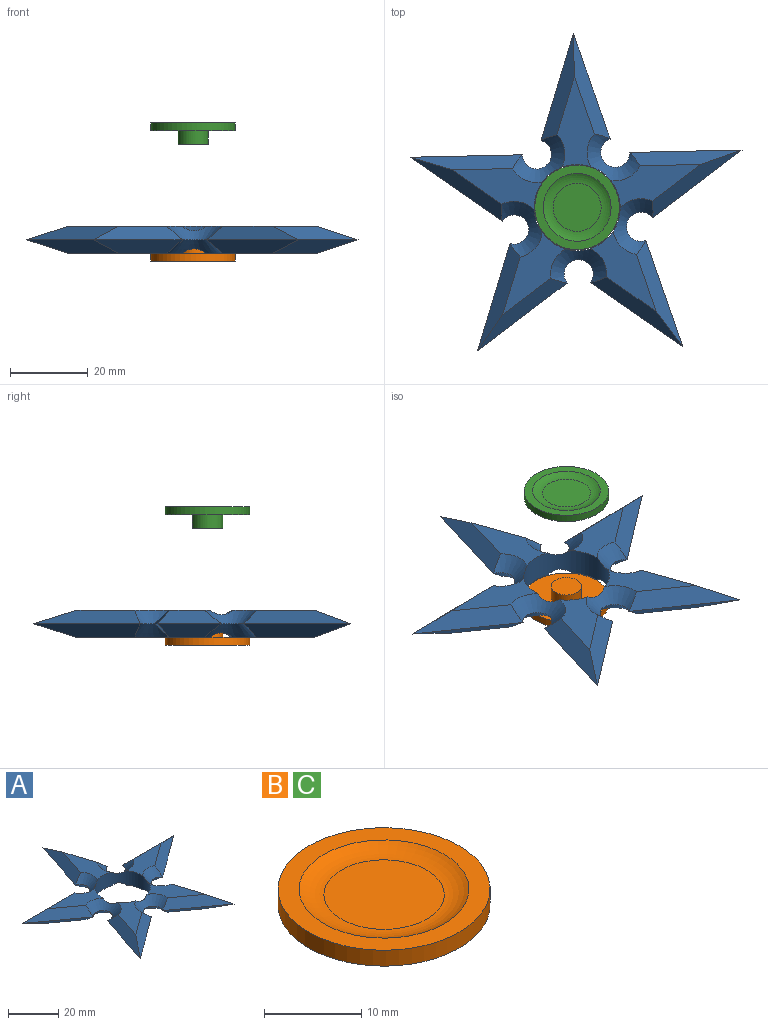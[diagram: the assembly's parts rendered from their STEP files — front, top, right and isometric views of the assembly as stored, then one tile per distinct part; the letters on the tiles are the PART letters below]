
ASSEMBLY  parts=3 mates=2
PART A: 41 faces, bbox 85.6x81.4x7 mm
  f0: plane 20.97x16.66mm, normal (0,0,-1), area 124.1mm2, adj f8,f27,f31,f35,f38
  f1: plane 23.23x10.72mm, normal (0,0,-1), area 124.1mm2, adj f8,f26,f30,f34,f38
  f2: plane 23.22x9.63mm, normal (0,0,-1), area 124.1mm2, adj f8,f14,f18,f22,f26
  f3: plane 23.23x10.72mm, normal (0,0,-1), area 124.1mm2, adj f8,f11,f12,f14,f15
  f4: plane 20.97x16.66mm, normal (0,0,1), area 124.1mm2, adj f8,f32,f36,f39,f40
  f5: plane 23.23x10.72mm, normal (0,0,1), area 124.1mm2, adj f8,f29,f33,f37,f40
  f6: plane 23.22x9.63mm, normal (0,0,1), area 124.1mm2, adj f8,f17,f21,f25,f29
  f7: plane 23.23x10.72mm, normal (0,0,1), area 124.1mm2, adj f8,f13,f16,f17,f20
  f8: cylinder r=11.1mm len=22.2mm, axis (0,0,-1), area 440mm2, adj f0,f1,f2,f3,f4,f5,f6,f7
  f9: plane 20.97x16.66mm, normal (0,0,1), area 124.1mm2, adj f8,f20,f24,f28,f32
  f10: plane 20.97x16.66mm, normal (0,0,-1), area 124.1mm2, adj f8,f15,f19,f23,f27
  f11: plane 28.94x3.5mm, normal (0,0.71,-0.71), area 109.6mm2, adj f3,f12,f13,f14
  f12: plane 23.42x17.01mm, normal (-0.42,-0.57,-0.71), area 109.6mm2, adj f3,f11,f15,f16
  f13: plane 28.94x3.5mm, normal (0,0.71,0.71), area 109.6mm2, adj f7,f11,f16,f17
  f14: cone r=7.25mm half-angle=45deg, axis (0,0,-1), area 95mm2, adj f2,f3,f8,f11,f17,f18
  f15: cone r=7.25mm half-angle=45deg, axis (0,0,-1), area 95mm2, adj f3,f8,f10,f12,f19,f20
  f16: plane 23.42x17.01mm, normal (-0.42,-0.57,0.71), area 109.6mm2, adj f7,f12,f13,f20
  f17: cone r=3.75mm half-angle=45deg, axis (0,0,1), area 95mm2, adj f6,f7,f8,f13,f14,f21
  f18: plane 27.53x8.94mm, normal (-0.67,0.22,-0.71), area 109.6mm2, adj f2,f14,f21,f22
  f19: plane 27.53x11.47mm, normal (-0.67,0.22,-0.71), area 109.6mm2, adj f10,f15,f23,f24
  f20: cone r=3.75mm half-angle=45deg, axis (0,0,1), area 95mm2, adj f7,f8,f9,f15,f16,f24
  f21: plane 27.53x8.94mm, normal (-0.67,0.22,0.71), area 109.6mm2, adj f6,f17,f18,f25
  f22: plane 27.53x8.94mm, normal (0.67,0.22,-0.71), area 109.6mm2, adj f2,f18,f25,f26
  f23: plane 23.42x18.32mm, normal (0.42,-0.57,-0.71), area 109.6mm2, adj f10,f19,f27,f28
  f24: plane 27.53x11.47mm, normal (-0.67,0.22,0.71), area 109.6mm2, adj f9,f19,f20,f28
  f25: plane 27.53x8.94mm, normal (0.67,0.22,0.71), area 109.6mm2, adj f6,f21,f22,f29
  f26: cone r=7.25mm half-angle=45deg, axis (0,0,-1), area 95mm2, adj f1,f2,f8,f22,f29,f30
  f27: cone r=7.25mm half-angle=45deg, axis (0,0,-1), area 95mm2, adj f0,f8,f10,f23,f31,f32
  f28: plane 23.42x18.32mm, normal (0.42,-0.57,0.71), area 109.6mm2, adj f9,f23,f24,f32
  f29: cone r=3.75mm half-angle=45deg, axis (0,0,1), area 95mm2, adj f5,f6,f8,f25,f26,f33
  f30: plane 28.94x3.5mm, normal (0,0.71,-0.71), area 109.6mm2, adj f1,f26,f33,f34
  f31: plane 23.42x18.32mm, normal (-0.42,-0.57,-0.71), area 109.6mm2, adj f0,f27,f35,f36
  f32: cone r=3.75mm half-angle=45deg, axis (0,0,1), area 95mm2, adj f4,f8,f9,f27,f28,f36
  f33: plane 28.94x3.5mm, normal (0,0.71,0.71), area 109.6mm2, adj f5,f29,f30,f37
  f34: plane 23.42x17.01mm, normal (0.42,-0.57,-0.71), area 109.6mm2, adj f1,f30,f37,f38
  f35: plane 27.53x11.47mm, normal (0.67,0.22,-0.71), area 109.6mm2, adj f0,f31,f38,f39
  f36: plane 23.42x18.32mm, normal (-0.42,-0.57,0.71), area 109.6mm2, adj f4,f31,f32,f39
  f37: plane 23.42x17.01mm, normal (0.42,-0.57,0.71), area 109.6mm2, adj f5,f33,f34,f40
  f38: cone r=7.25mm half-angle=45deg, axis (0,0,-1), area 95mm2, adj f0,f1,f8,f34,f35,f40
  f39: plane 27.53x11.47mm, normal (0.67,0.22,0.71), area 109.6mm2, adj f4,f35,f36,f40
  f40: cone r=3.75mm half-angle=45deg, axis (0,0,1), area 95mm2, adj f4,f5,f8,f37,f38,f39
PART B: 7 faces, bbox 21.8x21.8x6.3 mm
  f0: cylinder r=3.9mm len=7.8mm, axis (0,0,-1), area 85.8mm2, adj f1,f4
  f1: plane 7.8x7.8mm, normal (0,0,-1), area 47.8mm2, adj f0
  f2: cylinder r=10.9mm len=21.8mm, axis (0,0,-1), area 137mm2, adj f3,f4
  f3: plane 21.8x21.8mm, normal (0,0,1), area 133.4mm2, adj f2,f6
  f4: plane 21.8x21.8mm, normal (0,0,-1), area 325.5mm2, adj f0,f2
  f5: plane 12.37x12.37mm, normal (0,0,1), area 120.2mm2, adj f6
  f6: torus R=6.19mm, axis (0,0,-1), area 126.1mm2, adj f3,f5
PART C: same geometry as B
PLACE A rot(axis=(0,0,-1),142.8deg) t=(-35.1,-8.26,0)mm
PLACE B rot(axis=(0.71,0.71,0),180deg) t=(-35.1,-8.26,0)mm fixed
PLACE C rot(axis=(-0.5,0.84,0.23),0deg) t=(-35.1,-8.26,24.62)mm
MATE slider B.f0 <-> C.f0  axis (0,0,1) through (-35.1,-8.26,0)mm
MATE revolute A.f8 <-> B.f0  axis (0,0,-1) through (-35.1,-8.26,0)mm
